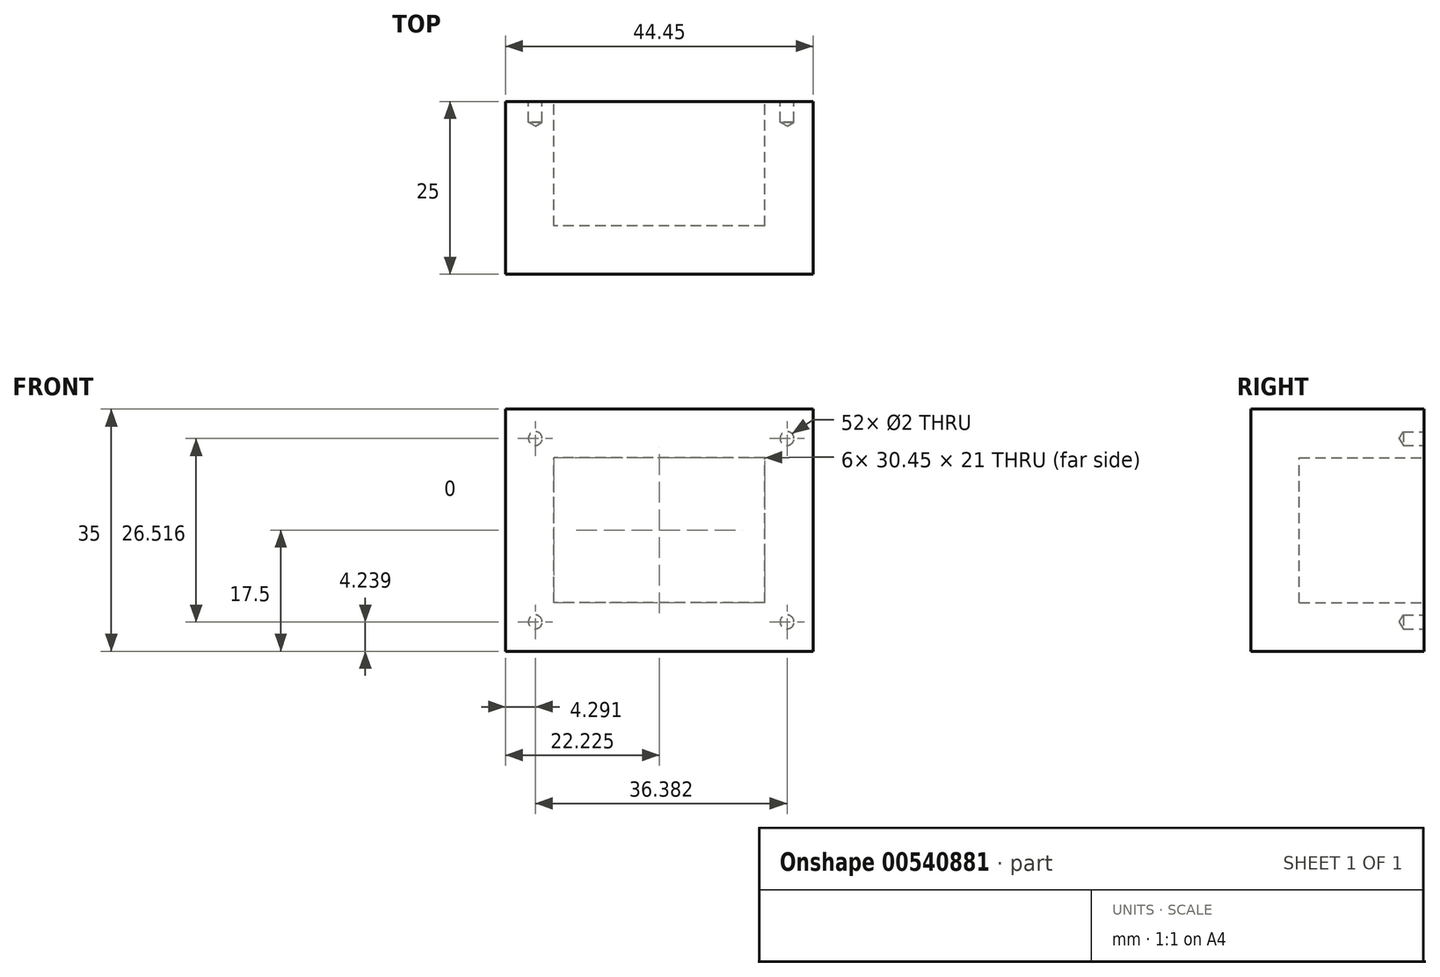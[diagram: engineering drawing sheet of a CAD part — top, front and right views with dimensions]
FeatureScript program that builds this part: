
annotation { "Feature Type Name" : "Feature", "Feature Type Description" : "" }
export const myFeature = defineFeature(function(context is Context, id is Id, definition is map)
    precondition{}
    {
        {
            var Q0;
            Q0=qCreatedBy(makeId("Front.planeOp"),FACE);
            var sketch = newSketch(context, id + "F0", { "sketchPlane" : qUnion([Q0])});
            skLineSegment(sketch, "E0.bottom", {"start": v(0, 0) * mm, "end": v(-44.45, 0) * mm});
            skLineSegment(sketch, "E0.top", {"start": v(0, 35) * mm, "end": v(-44.45, 35) * mm});
            skLineSegment(sketch, "E0.left", {"start": v(0, 0) * mm, "end": v(0, 35) * mm});
            skLineSegment(sketch, "E0.right", {"start": v(-44.45, 0) * mm, "end": v(-44.45, 35) * mm});
            skPoint(sketch, "E1", {"position": v(-3.78, 30.76) * mm});
            skPoint(sketch, "E2", {"position": v(-3.78, 4.24) * mm});
            skPoint(sketch, "E3", {"position": v(-40.16, 4.24) * mm});
            skPoint(sketch, "E4", {"position": v(-40.16, 30.76) * mm});
            skSolve(sketch);
        }
        {
            var Q0;
            Q0=makeQuery(id+"F0.imprint","IMPRINT",FACE,{"disambiguationData":[TD([[makeQuery(id+"F0.imprint","IMPRINT",EDGE,{"derivedFrom":sQuery(id+"F0.wireOp",EDGE,"E0.bottom")}),-1.0]])]});
            extrude(context, id + "F1", {"entities" : qUnion([Q0]), "depth" : 25 * mm, "offsetDistance" : 25.4 * mm});
        }
        {
            var Q0;
            Q0=makeQuery(id+"F1.opExtrude","CAP_FACE",FACE,{"disambiguationData":[OSD([sQuery(id+"F0.wireOp",EDGE,"E0.bottom"),sQuery(id+"F0.wireOp",EDGE,"E0.top"),sQuery(id+"F0.wireOp",EDGE,"E0.left"),sQuery(id+"F0.wireOp",EDGE,"E0.right")])],"isStart":true});
            shell(context, id + "F2", {"entities" : qUnion([Q0]), "thickness" : 7 * mm});
        }
        {
            var Q0;
            Q0=sQuery(id+"F0.wireOp",VERTEX,"E1");
            var Q1;
            Q1=sQuery(id+"F0.wireOp",VERTEX,"E4");
            var Q2;
            Q2=sQuery(id+"F0.wireOp",VERTEX,"E3");
            var Q3;
            Q3=sQuery(id+"F0.wireOp",VERTEX,"E2");
            var Q4;
            Q4=makeQuery(id+"F1.opExtrude","SWEPT_BODY",BODY,{"disambiguationData":[OSD([sQuery(id+"F0.wireOp",EDGE,"E0.bottom"),sQuery(id+"F0.wireOp",EDGE,"E0.top"),sQuery(id+"F0.wireOp",EDGE,"E0.left"),sQuery(id+"F0.wireOp",EDGE,"E0.right")])]});
            hole(context, id + "F3", {"style" : HoleStyle.SIMPLE, "endStyle" : HoleEndStyle.BLIND, "oppositeDirection" : true, "holeDiameter" : 2 * mm, "majorDiameter" : 6.35 * mm, "holeDepth" : 3 * mm, "isTappedThrough" : true, "tappedDepth" : 12.7 * mm, "tapClearance" : 3, "locations" : qUnion([Q0, Q1, Q2, Q3]), "scope" : qUnion([Q4])});
        }
    });
